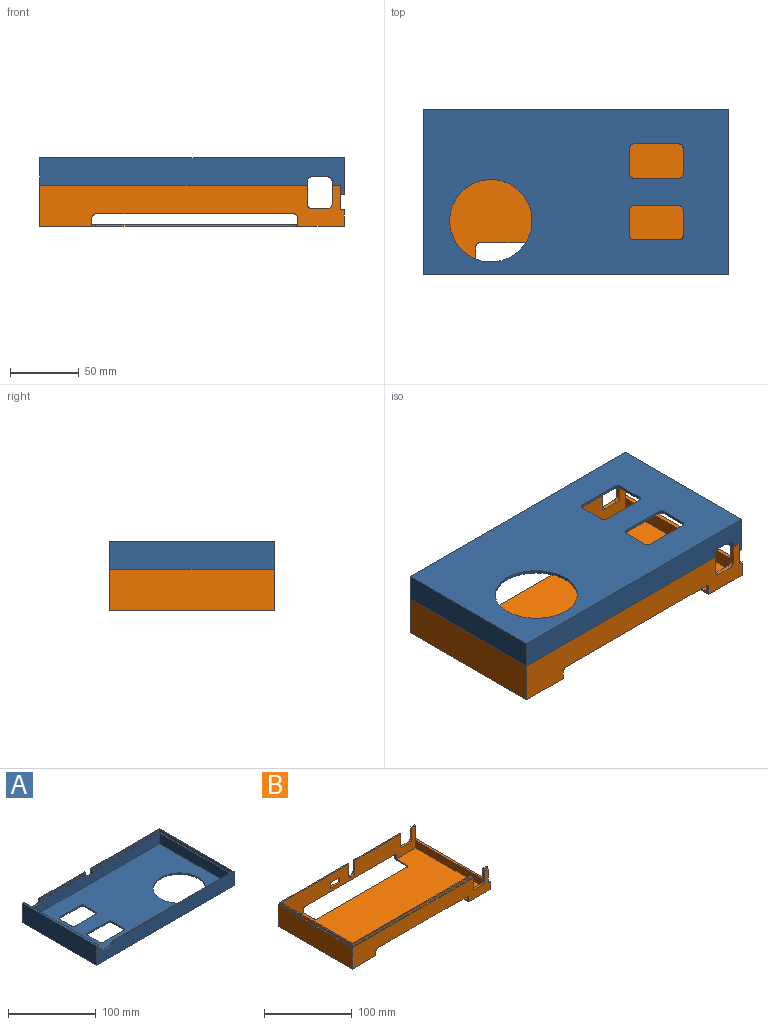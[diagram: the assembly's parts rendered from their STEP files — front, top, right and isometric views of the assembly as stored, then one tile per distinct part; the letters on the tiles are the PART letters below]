
ASSEMBLY  parts=2 mates=1
PART A: 57 faces, bbox 222x120x27 mm
  f0: plane 6x1.4mm, normal (0,0,1), area 8.4mm2, adj f5,f9,f23,f52
  f1: plane 216x15mm, normal (0,-1,0), area 3143.7mm2, adj f3,f22,f23,f26,f30,f31,f32,f33
  f2: plane 216x15mm, normal (0,1,0), area 3189.9mm2, adj f3,f22,f23,f29,f35,f36,f51,f53
  f3: plane 114x15mm, normal (-1,0,0), area 1710mm2, adj f1,f2,f22,f53
  f4: plane 3x1.4mm, normal (-1,0,0), area 4.2mm2, adj f7,f9,f35,f56
  f5: plane 3x1.4mm, normal (1,0,0), area 4.2mm2, adj f0,f9,f36,f52
  f6: plane 74x1.4mm, normal (0,0,1), area 103.6mm2, adj f11,f28,f32,f50
  f7: plane 195x120mm, normal (0,0,1), area 592.5mm2, adj f4,f9,f10,f11,f31,f54,f55,f56
  f8: plane 6x1.4mm, normal (0,0,1), area 8.4mm2, adj f11,f23,f27,f48
  f9: plane 222x27mm, normal (0,-1,0), area 4356.9mm2, adj f0,f4,f5,f7,f10,f12,f23,f24
  f10: plane 120x20mm, normal (1,0,0), area 2400mm2, adj f7,f9,f11,f12
  f11: plane 222x27mm, normal (0,1,0), area 4280.7mm2, adj f6,f7,f8,f10,f12,f23,f24,f25
  f12: plane 222x120mm, normal (0,0,-1), area 21878mm2, adj f9,f10,f11,f13,f14,f15,f16,f17
  f13: plane 19x2mm, normal (1,0,0), area 38mm2, adj f12,f22,f43,f46
  f14: plane 33x2mm, normal (0,-1,0), area 66mm2, adj f12,f22,f43,f44
  f15: plane 19x2mm, normal (-1,0,0), area 38mm2, adj f12,f22,f44,f45
  f16: plane 19x2mm, normal (1,0,0), area 38mm2, adj f12,f22,f39,f42
  f17: plane 33x2mm, normal (0,-1,0), area 66mm2, adj f12,f22,f39,f40
  f18: plane 19x2mm, normal (-1,0,0), area 38mm2, adj f12,f22,f40,f41
  f19: cylinder r=30mm len=60mm, axis (0,0,-1), area 377mm2, adj f12,f22
  f20: plane 33x2mm, normal (0,1,0), area 66mm2, adj f12,f22,f45,f46
  f21: plane 33x2mm, normal (0,1,0), area 66mm2, adj f12,f22,f41,f42
  f22: plane 216x114mm, normal (0,0,1), area 19862mm2, adj f1,f2,f3,f13,f14,f15,f16,f17
  f23: plane 120x25mm, normal (1,0,0), area 2901.6mm2, adj f0,f1,f2,f8,f9,f11,f22,f25
  f24: plane 120x27mm, normal (-1,0,0), area 3240mm2, adj f9,f11,f12,f25
  f25: plane 120x3mm, normal (0,0,1), area 360mm2, adj f9,f11,f23,f24
  f26: plane 12x3mm, normal (0,0,1), area 36mm2, adj f1,f11,f37,f38
  f27: plane 3x1.4mm, normal (1,0,0), area 4.2mm2, adj f8,f11,f38,f48
  f28: plane 3x1.4mm, normal (-1,0,0), area 4.2mm2, adj f6,f11,f37,f50
  f29: plane 12x3mm, normal (0,0,1), area 36mm2, adj f2,f9,f35,f36
  f30: plane 4x3mm, normal (0,0,1), area 12mm2, adj f1,f11,f33,f34
  f31: plane 5x3mm, normal (-1,0,0), area 10.2mm2, adj f1,f7,f11,f34,f53,f55
  f32: plane 5x3mm, normal (1,0,0), area 10.2mm2, adj f1,f6,f11,f33,f49,f50
  f33: cylinder r=3mm len=3mm, axis (0,1,0), area 14.1mm2, adj f1,f11,f30,f32
  f34: cylinder r=3mm len=3mm, axis (0,-1,0), area 14.1mm2, adj f1,f11,f30,f31
  f35: cylinder r=3mm len=3mm, axis (0,1,0), area 14.1mm2, adj f2,f4,f9,f29,f53
  f36: cylinder r=3mm len=3mm, axis (0,-1,0), area 14.1mm2, adj f2,f5,f9,f29,f51
  f37: cylinder r=3mm len=3mm, axis (0,1,0), area 14.1mm2, adj f1,f11,f26,f28,f49
  f38: cylinder r=3mm len=3mm, axis (0,-1,0), area 14.1mm2, adj f1,f11,f26,f27,f47
  f39: cylinder r=3mm len=3mm, axis (0,0,-1), area 9.4mm2, adj f12,f16,f17,f22
  f40: cylinder r=3mm len=3mm, axis (0,0,1), area 9.4mm2, adj f12,f17,f18,f22
  f41: cylinder r=3mm len=3mm, axis (0,0,-1), area 9.4mm2, adj f12,f18,f21,f22
  f42: cylinder r=3mm len=3mm, axis (0,0,1), area 9.4mm2, adj f12,f16,f21,f22
  f43: cylinder r=3mm len=3mm, axis (0,0,-1), area 9.4mm2, adj f12,f13,f14,f22
  f44: cylinder r=3mm len=3mm, axis (0,0,1), area 9.4mm2, adj f12,f14,f15,f22
  f45: cylinder r=3mm len=3mm, axis (0,0,-1), area 9.4mm2, adj f12,f15,f20,f22
  f46: cylinder r=3mm len=3mm, axis (0,0,1), area 9.4mm2, adj f12,f13,f20,f22
  f47: plane 6x1.6mm, normal (0,0,1), area 9.6mm2, adj f1,f23,f38,f48
  f48: plane 6x3mm, normal (0,-1,0), area 18mm2, adj f8,f23,f27,f47
  f49: plane 74x1.6mm, normal (0,0,1), area 118.4mm2, adj f1,f32,f37,f50
  f50: plane 74x3mm, normal (0,-1,0), area 222mm2, adj f6,f28,f32,f49
  f51: plane 6x1.6mm, normal (0,0,1), area 9.6mm2, adj f2,f23,f36,f52
  f52: plane 6x3mm, normal (0,1,0), area 18mm2, adj f0,f5,f23,f51
  f53: plane 193.6x117.2mm, normal (0,0,1), area 667.5mm2, adj f1,f2,f3,f31,f35,f54,f55,f56
  f54: plane 117.2x3mm, normal (-1,0,0), area 351.6mm2, adj f7,f53,f55,f56
  f55: plane 109.6x3mm, normal (0,-1,0), area 328.8mm2, adj f7,f31,f53,f54
  f56: plane 193.6x3mm, normal (0,1,0), area 580.8mm2, adj f4,f7,f53,f54
PART B: 192 faces, bbox 222x120x33 mm
  f0: plane 6x1.45mm, normal (0,0,1), area 8.7mm2, adj f3,f4,f26,f188
  f1: plane 74x1.45mm, normal (0,0,1), area 107.3mm2, adj f3,f27,f29,f186
  f2: plane 195x120mm, normal (0,0,1), area 613.5mm2, adj f3,f9,f10,f23,f30,f182,f183,f184
  f3: plane 222x30mm, normal (0,1,0), area 4636.3mm2, adj f0,f1,f2,f4,f8,f9,f14,f16
  f4: plane 21x3mm, normal (1,0,0), area 58.6mm2, adj f0,f3,f5,f37,f188,f189
  f5: plane 216x31.5mm, normal (0,-1,0), area 5015.6mm2, adj f4,f12,f14,f16,f19,f21,f25,f26
  f6: plane 216x31.5mm, normal (0,1,0), area 5326.7mm2, adj f11,f12,f13,f17,f19,f20,f22,f23
  f7: plane 6x1.45mm, normal (0,0,1), area 8.7mm2, adj f10,f11,f24,f190
  f8: plane 222x120mm, normal (0,0,-1), area 19747.7mm2, adj f3,f9,f10,f13,f14,f15,f16,f17
  f9: plane 120x30mm, normal (-1,0,0), area 3600mm2, adj f2,f3,f8,f10
  f10: plane 222x30mm, normal (0,-1,0), area 4957.7mm2, adj f2,f7,f8,f9,f11,f13,f17,f20
  f11: plane 21x3mm, normal (1,0,0), area 58.6mm2, adj f6,f7,f10,f37,f190,f191
  f12: plane 114x31.5mm, normal (1,0,0), area 3591mm2, adj f5,f6,f19,f185
  f13: plane 20x6mm, normal (-1,0,0), area 43.5mm2, adj f6,f8,f10,f19,f44,f51
  f14: plane 20x6mm, normal (-1,0,0), area 43.5mm2, adj f3,f5,f8,f19,f46,f48
  f15: plane 144x1.5mm, normal (0,1,0), area 216mm2, adj f8,f19,f48,f49
  f16: plane 20x6mm, normal (1,0,0), area 43.5mm2, adj f3,f5,f8,f19,f47,f49
  f17: plane 20x6mm, normal (1,0,0), area 43.5mm2, adj f6,f8,f10,f19,f45,f50
  f18: plane 144x1.5mm, normal (0,-1,0), area 216mm2, adj f8,f19,f50,f51
  f19: plane 216x114mm, normal (0,0,1), area 18631.7mm2, adj f5,f6,f12,f13,f14,f15,f16,f17
  f20: plane 144x3mm, normal (0,0,-1), area 432mm2, adj f6,f10,f44,f45
  f21: plane 144x3mm, normal (0,0,-1), area 432mm2, adj f3,f5,f46,f47
  f22: plane 12x3mm, normal (0,0,1), area 36mm2, adj f6,f10,f40,f41
  f23: plane 17x3mm, normal (1,0,0), area 46.7mm2, adj f2,f6,f10,f41,f184,f185
  f24: plane 17x3mm, normal (-1,0,0), area 46.7mm2, adj f6,f7,f10,f40,f190,f191
  f25: plane 12x3mm, normal (0,0,1), area 36mm2, adj f3,f5,f42,f43
  f26: plane 17x3mm, normal (-1,0,0), area 46.6mm2, adj f0,f3,f5,f42,f188,f189
  f27: plane 17x3mm, normal (1,0,0), area 46.6mm2, adj f1,f3,f5,f43,f186,f187
  f28: plane 4x3mm, normal (0,0,1), area 12mm2, adj f3,f5,f38,f39
  f29: plane 16.5x3mm, normal (-1,0,0), area 45.2mm2, adj f1,f3,f5,f39,f186,f187
  f30: plane 16.5x3mm, normal (1,0,0), area 45.2mm2, adj f2,f3,f5,f38,f182,f185
  f31: plane 8x3mm, normal (1,0,0), area 24mm2, adj f3,f5,f32,f34
  f32: plane 15x3mm, normal (0,0,-1), area 45mm2, adj f3,f5,f31,f33
  f33: plane 8x3mm, normal (-1,0,0), area 24mm2, adj f3,f5,f32,f34
  f34: plane 15x3mm, normal (0,0,1), area 45mm2, adj f3,f5,f31,f33
  f35: plane 114x10.5mm, normal (-1,0,0), area 1197mm2, adj f5,f6,f19,f37
  f36: plane 120x12mm, normal (1,0,0), area 1440mm2, adj f3,f8,f10,f37
  f37: plane 120x3mm, normal (0,0,1), area 360mm2, adj f3,f4,f10,f11,f35,f36
  f38: cylinder r=3mm len=3mm, axis (0,1,0), area 14.1mm2, adj f3,f5,f28,f30
  f39: cylinder r=3mm len=3mm, axis (0,-1,0), area 14.1mm2, adj f3,f5,f28,f29
  f40: cylinder r=3mm len=3mm, axis (0,1,0), area 14.1mm2, adj f6,f10,f22,f24
  f41: cylinder r=3mm len=3mm, axis (0,-1,0), area 14.1mm2, adj f6,f10,f22,f23
  f42: cylinder r=3mm len=3mm, axis (0,1,0), area 14.1mm2, adj f3,f5,f25,f26
  f43: cylinder r=3mm len=3mm, axis (0,-1,0), area 14.1mm2, adj f3,f5,f25,f27
  f44: cylinder r=3mm len=3mm, axis (0,1,0), area 14.1mm2, adj f6,f10,f13,f20
  f45: cylinder r=3mm len=3mm, axis (0,-1,0), area 14.1mm2, adj f6,f10,f17,f20
  f46: cylinder r=3mm len=3mm, axis (0,1,0), area 14.1mm2, adj f3,f5,f14,f21
  f47: cylinder r=3mm len=3mm, axis (0,-1,0), area 14.1mm2, adj f3,f5,f16,f21
  f48: cylinder r=3mm len=3mm, axis (0,0,-1), area 7.1mm2, adj f8,f14,f15,f19
  f49: cylinder r=3mm len=3mm, axis (0,0,1), area 7.1mm2, adj f8,f15,f16,f19
  f50: cylinder r=3mm len=3mm, axis (0,0,-1), area 7.1mm2, adj f8,f17,f18,f19
  f51: cylinder r=3mm len=3mm, axis (0,0,1), area 7.1mm2, adj f8,f13,f18,f19
  f52: extruded ~1x0.93mm, area 0.9mm2, adj f53,f67,f68,f180
  f53: extruded ~1x0.93mm, area 0.9mm2, adj f52,f54,f68,f180
  f54: extruded ~1x0.38mm, area 0.5mm2, adj f53,f55,f68,f180
  f55: extruded ~1x0.38mm, area 0.5mm2, adj f54,f56,f68,f180
  f56: extruded ~1x0.93mm, area 0.9mm2, adj f55,f57,f68,f180
  f57: extruded ~1x0.93mm, area 0.9mm2, adj f56,f58,f68,f180
  f58: extruded ~1x0.38mm, area 0.5mm2, adj f57,f67,f68,f180
  f59: extruded ~1.37x1mm, area 1.4mm2, adj f3,f60,f66,f68
  f60: extruded ~1.36x1mm, area 1.4mm2, adj f3,f59,f61,f68
  f61: extruded ~1x0.92mm, area 1.1mm2, adj f3,f60,f62,f68
  f62: extruded ~1x0.93mm, area 1.1mm2, adj f3,f61,f63,f68
  f63: extruded ~1.38x1mm, area 1.4mm2, adj f3,f62,f64,f68
  f64: extruded ~1.35x1mm, area 1.4mm2, adj f3,f63,f65,f68
  f65: extruded ~1x0.92mm, area 1.1mm2, adj f3,f64,f66,f68
  f66: extruded ~1x0.93mm, area 1.1mm2, adj f3,f59,f65,f68
  f67: extruded ~1x0.38mm, area 0.5mm2, adj f52,f58,f68,f180
  f68: plane 3.63x2.47mm, normal (0,1,0), area 5.5mm2, adj f52,f53,f54,f55,f56,f57,f58,f59
  f69: plane 2.47x1mm, normal (0,0,1), area 2.5mm2, adj f3,f70,f92,f93
  f70: plane 1x0.63mm, normal (1,0,0), area 0.6mm2, adj f3,f69,f71,f93
  f71: plane 1.54x1mm, normal (0,0,-1), area 1.5mm2, adj f3,f70,f72,f93
  f72: plane 1x0.03mm, normal (1,0,0), area 0mm2, adj f3,f71,f73,f93
  f73: plane 1x0.45mm, normal (0.69,0,0.73), area 0.6mm2, adj f3,f72,f74,f93
  f74: extruded ~1x0.64mm, area 0.9mm2, adj f3,f73,f75,f93
  f75: extruded ~1x0.44mm, area 0.5mm2, adj f3,f74,f76,f93
  f76: extruded ~1x0.46mm, area 0.5mm2, adj f3,f75,f77,f93
  f77: extruded ~1x0.5mm, area 0.5mm2, adj f3,f76,f78,f93
  f78: extruded ~1x0.39mm, area 0.5mm2, adj f3,f77,f79,f93
  f79: extruded ~1x0.58mm, area 0.6mm2, adj f3,f78,f80,f93
  f80: extruded ~1x0.45mm, area 0.5mm2, adj f3,f79,f81,f93
  f81: extruded ~1x0.37mm, area 0.4mm2, adj f3,f80,f82,f93
  f82: extruded ~1x0.43mm, area 0.5mm2, adj f3,f81,f83,f93
  f83: plane 1x0.48mm, normal (-0.76,0,0.65), area 0.6mm2, adj f3,f82,f84,f93
  f84: extruded ~1x0.4mm, area 0.5mm2, adj f3,f83,f85,f93
  f85: extruded ~1x0.4mm, area 0.4mm2, adj f3,f84,f86,f93
  f86: extruded ~1x0.31mm, area 0.3mm2, adj f3,f85,f87,f93
  f87: extruded ~1x0.32mm, area 0.3mm2, adj f3,f86,f88,f93
  f88: extruded ~1x0.28mm, area 0.3mm2, adj f3,f87,f89,f93
  f89: extruded ~1x0.29mm, area 0.3mm2, adj f3,f88,f90,f93
  f90: extruded ~1x0.56mm, area 0.8mm2, adj f3,f89,f91,f93
  f91: plane 1x0.9mm, normal (-0.71,0,-0.7), area 1.3mm2, adj f3,f90,f92,f93
  f92: plane 1x0.52mm, normal (-1,0,0), area 0.5mm2, adj f3,f69,f91,f93
  f93: plane 3.58x2.48mm, normal (0,1,0), area 4.6mm2, adj f69,f70,f71,f72,f73,f74,f75,f76
  f94: plane 1x0.75mm, normal (0,0,1), area 0.7mm2, adj f3,f95,f103,f104
  f95: plane 3.53x1mm, normal (1,0,0), area 3.5mm2, adj f3,f94,f96,f104
  f96: plane 1x0.61mm, normal (0,0,-1), area 0.6mm2, adj f3,f95,f97,f104
  f97: plane 1.14x1mm, normal (-0.62,0,-0.78), area 1.5mm2, adj f3,f96,f98,f104
  f98: plane 1x0.45mm, normal (-0.78,0,0.63), area 0.6mm2, adj f3,f97,f99,f104
  f99: plane 1x0.41mm, normal (0.63,0,0.78), area 0.5mm2, adj f3,f98,f100,f104
  f100: extruded ~1x0.26mm, area 0.4mm2, adj f3,f99,f101,f104
  f101: plane 1x0.37mm, normal (-1,0,-0.03), area 0.4mm2, adj f3,f100,f102,f104
  f102: plane 1x0.34mm, normal (-1,0,-0.02), area 0.3mm2, adj f3,f101,f103,f104
  f103: plane 2.04x1mm, normal (-1,0,0), area 2mm2, adj f3,f94,f102,f104
  f104: plane 3.53x1.75mm, normal (0,1,0), area 3.2mm2, adj f94,f95,f96,f97,f98,f99,f100,f101
  f105: plane 1x0.75mm, normal (0,0,1), area 0.7mm2, adj f3,f106,f114,f115
  f106: plane 3.53x1mm, normal (1,0,0), area 3.5mm2, adj f3,f105,f107,f115
  f107: plane 1x0.61mm, normal (0,0,-1), area 0.6mm2, adj f3,f106,f108,f115
  f108: plane 1.14x1mm, normal (-0.62,0,-0.78), area 1.5mm2, adj f3,f107,f109,f115
  f109: plane 1x0.45mm, normal (-0.78,0,0.63), area 0.6mm2, adj f3,f108,f110,f115
  f110: plane 1x0.41mm, normal (0.63,0,0.78), area 0.5mm2, adj f3,f109,f111,f115
  f111: extruded ~1x0.26mm, area 0.4mm2, adj f3,f110,f112,f115
  f112: plane 1x0.37mm, normal (-1,0,-0.03), area 0.4mm2, adj f3,f111,f113,f115
  f113: plane 1x0.34mm, normal (-1,0,-0.02), area 0.3mm2, adj f3,f112,f114,f115
  f114: plane 2.04x1mm, normal (-1,0,0), area 2mm2, adj f3,f105,f113,f115
  f115: plane 3.53x1.75mm, normal (0,1,0), area 3.2mm2, adj f105,f106,f107,f108,f109,f110,f111,f112
  f116: plane 1x0.76mm, normal (0,0,-1), area 0.8mm2, adj f3,f117,f125,f126
  f117: plane 2.1x1mm, normal (-0.95,0,-0.3), area 2.2mm2, adj f3,f116,f118,f126
  f118: extruded ~1x0.78mm, area 0.8mm2, adj f3,f117,f119,f126
  f119: extruded ~1x0.34mm, area 0.4mm2, adj f3,f118,f120,f126
  f120: extruded ~1x0.43mm, area 0.4mm2, adj f3,f119,f121,f126
  f121: plane 2.1x1mm, normal (0.95,0,-0.3), area 2.2mm2, adj f3,f120,f122,f126
  f122: plane 1x0.76mm, normal (0,0,-1), area 0.8mm2, adj f3,f121,f123,f126
  f123: plane 3.53x1.2mm, normal (-0.95,0,0.32), area 3.7mm2, adj f3,f122,f124,f126
  f124: plane 1x0.82mm, normal (0,0,1), area 0.8mm2, adj f3,f123,f125,f126
  f125: plane 3.53x1.2mm, normal (0.95,0,0.32), area 3.7mm2, adj f3,f116,f124,f126
  f126: plane 3.53x3.21mm, normal (0,1,0), area 4.8mm2, adj f116,f117,f118,f119,f120,f121,f122,f123
  f127: plane 2.47x1mm, normal (0,0,1), area 2.5mm2, adj f3,f128,f150,f151
  f128: plane 1x0.63mm, normal (1,0,0), area 0.6mm2, adj f3,f127,f129,f151
  f129: plane 1.54x1mm, normal (0,0,-1), area 1.5mm2, adj f3,f128,f130,f151
  f130: plane 1x0.03mm, normal (1,0,0), area 0mm2, adj f3,f129,f131,f151
  f131: plane 1x0.45mm, normal (0.69,0,0.73), area 0.6mm2, adj f3,f130,f132,f151
  f132: extruded ~1x0.64mm, area 0.9mm2, adj f3,f131,f133,f151
  f133: extruded ~1x0.44mm, area 0.5mm2, adj f3,f132,f134,f151
  f134: extruded ~1x0.46mm, area 0.5mm2, adj f3,f133,f135,f151
  f135: extruded ~1x0.5mm, area 0.5mm2, adj f3,f134,f136,f151
  f136: extruded ~1x0.39mm, area 0.5mm2, adj f3,f135,f137,f151
  f137: extruded ~1x0.58mm, area 0.6mm2, adj f3,f136,f138,f151
  f138: extruded ~1x0.45mm, area 0.5mm2, adj f3,f137,f139,f151
  f139: extruded ~1x0.37mm, area 0.4mm2, adj f3,f138,f140,f151
  f140: extruded ~1x0.43mm, area 0.5mm2, adj f3,f139,f141,f151
  f141: plane 1x0.48mm, normal (-0.76,0,0.65), area 0.6mm2, adj f3,f140,f142,f151
  f142: extruded ~1x0.4mm, area 0.5mm2, adj f3,f141,f143,f151
  f143: extruded ~1x0.4mm, area 0.4mm2, adj f3,f142,f144,f151
  f144: extruded ~1x0.31mm, area 0.3mm2, adj f3,f143,f145,f151
  f145: extruded ~1x0.32mm, area 0.3mm2, adj f3,f144,f146,f151
  f146: extruded ~1x0.28mm, area 0.3mm2, adj f3,f145,f147,f151
  f147: extruded ~1x0.29mm, area 0.3mm2, adj f3,f146,f148,f151
  f148: extruded ~1x0.56mm, area 0.8mm2, adj f3,f147,f149,f151
  f149: plane 1x0.9mm, normal (-0.71,0,-0.7), area 1.3mm2, adj f3,f148,f150,f151
  f150: plane 1x0.52mm, normal (-1,0,0), area 0.5mm2, adj f3,f127,f149,f151
  f151: plane 3.58x2.48mm, normal (0,1,0), area 4.6mm2, adj f127,f128,f129,f130,f131,f132,f133,f134
  f152: extruded ~1x0.93mm, area 0.9mm2, adj f153,f167,f168,f181
  f153: extruded ~1x0.93mm, area 0.9mm2, adj f152,f154,f168,f181
  f154: extruded ~1x0.38mm, area 0.5mm2, adj f153,f155,f168,f181
  f155: extruded ~1x0.38mm, area 0.5mm2, adj f154,f156,f168,f181
  f156: extruded ~1x0.93mm, area 0.9mm2, adj f155,f157,f168,f181
  f157: extruded ~1x0.93mm, area 0.9mm2, adj f156,f158,f168,f181
  f158: extruded ~1x0.38mm, area 0.5mm2, adj f157,f167,f168,f181
  f159: extruded ~1.37x1mm, area 1.4mm2, adj f3,f160,f166,f168
  f160: extruded ~1.36x1mm, area 1.4mm2, adj f3,f159,f161,f168
  f161: extruded ~1x0.92mm, area 1.1mm2, adj f3,f160,f162,f168
  f162: extruded ~1x0.93mm, area 1.1mm2, adj f3,f161,f163,f168
  f163: extruded ~1.38x1mm, area 1.4mm2, adj f3,f162,f164,f168
  f164: extruded ~1.35x1mm, area 1.4mm2, adj f3,f163,f165,f168
  f165: extruded ~1x0.92mm, area 1.1mm2, adj f3,f164,f166,f168
  f166: extruded ~1x0.93mm, area 1.1mm2, adj f3,f159,f165,f168
  f167: extruded ~1x0.38mm, area 0.5mm2, adj f152,f158,f168,f181
  f168: plane 3.63x2.47mm, normal (0,1,0), area 5.5mm2, adj f152,f153,f154,f155,f156,f157,f158,f159
  f169: plane 1x0.76mm, normal (0,0,-1), area 0.8mm2, adj f3,f170,f178,f179
  f170: plane 2.1x1mm, normal (-0.95,0,-0.3), area 2.2mm2, adj f3,f169,f171,f179
  f171: extruded ~1x0.78mm, area 0.8mm2, adj f3,f170,f172,f179
  f172: extruded ~1x0.34mm, area 0.4mm2, adj f3,f171,f173,f179
  f173: extruded ~1x0.43mm, area 0.4mm2, adj f3,f172,f174,f179
  f174: plane 2.1x1mm, normal (0.95,0,-0.3), area 2.2mm2, adj f3,f173,f175,f179
  f175: plane 1x0.76mm, normal (0,0,-1), area 0.8mm2, adj f3,f174,f176,f179
  f176: plane 3.53x1.2mm, normal (-0.95,0,0.32), area 3.7mm2, adj f3,f175,f177,f179
  f177: plane 1x0.82mm, normal (0,0,1), area 0.8mm2, adj f3,f176,f178,f179
  f178: plane 3.53x1.2mm, normal (0.95,0,0.32), area 3.7mm2, adj f3,f169,f177,f179
  f179: plane 3.53x3.21mm, normal (0,1,0), area 4.8mm2, adj f169,f170,f171,f172,f173,f174,f175,f176
  f180: plane 2.43x0.98mm, normal (0,1,0), area 2mm2, adj f52,f53,f54,f55,f56,f57,f58,f67
  f181: plane 2.43x0.98mm, normal (0,1,0), area 2mm2, adj f152,f153,f154,f155,f156,f157,f158,f167
  f182: plane 109.55x3mm, normal (0,1,0), area 328.7mm2, adj f2,f30,f183,f185
  f183: plane 117.1x3mm, normal (-1,0,0), area 351.3mm2, adj f2,f182,f184,f185
  f184: plane 193.55x3mm, normal (0,-1,0), area 580.7mm2, adj f2,f23,f183,f185
  f185: plane 193.55x117.1mm, normal (0,0,1), area 646.5mm2, adj f5,f6,f12,f23,f30,f182,f183,f184
  f186: plane 74x3mm, normal (0,1,0), area 222mm2, adj f1,f27,f29,f187
  f187: plane 74x1.55mm, normal (0,0,1), area 114.7mm2, adj f5,f27,f29,f186
  f188: plane 6x3mm, normal (0,1,0), area 18mm2, adj f0,f4,f26,f189
  f189: plane 6x1.55mm, normal (0,0,1), area 9.3mm2, adj f4,f5,f26,f188
  f190: plane 6x3mm, normal (0,-1,0), area 18mm2, adj f7,f11,f24,f191
  f191: plane 6x1.55mm, normal (0,0,1), area 9.3mm2, adj f6,f11,f24,f190
PLACE A rot(axis=(0,1,0),180deg) t=(-1.77,4.44,102.59)mm
PLACE B t=(-1.77,4.44,52.59)mm fixed
MATE slider A.f7 <-> B.f2  axis (0,0,-1) through (-112.77,-55.56,82.59)mm
